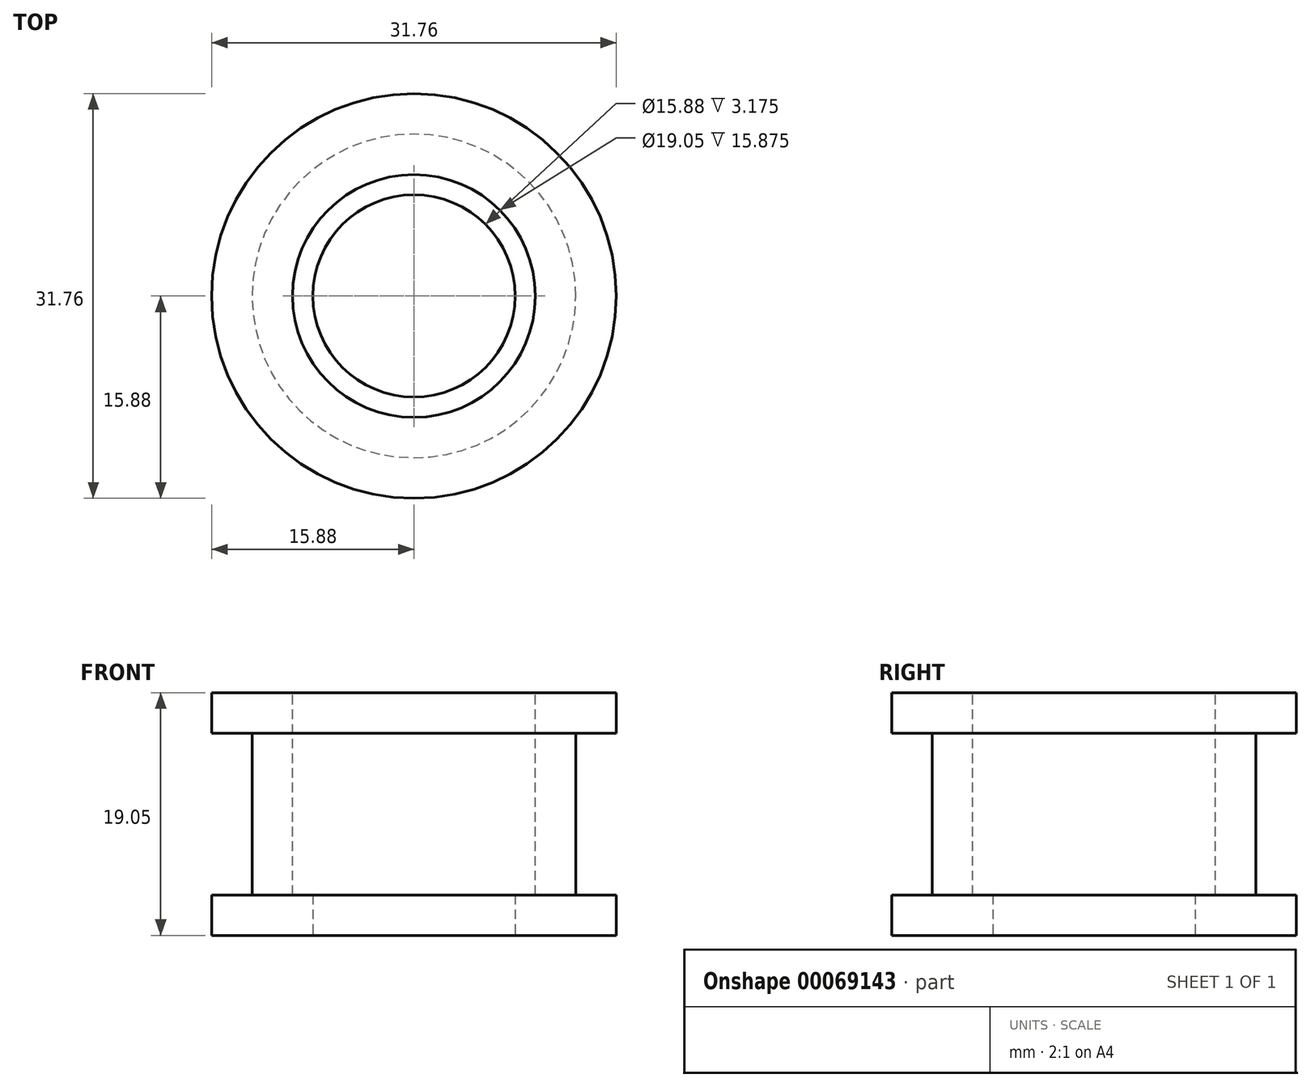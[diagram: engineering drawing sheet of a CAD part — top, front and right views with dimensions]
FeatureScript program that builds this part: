
annotation { "Feature Type Name" : "Feature", "Feature Type Description" : "" }
export const myFeature = defineFeature(function(context is Context, id is Id, definition is map)
    precondition{}
    {
        {
            var Q0;
            Q0=qCreatedBy(makeId("Top.planeOp"),FACE);
            var sketch = newSketch(context, id + "F0", { "sketchPlane" : qUnion([Q0])});
            skCircle(sketch, "E0", {"center": v(0, 0) * mm, "radius": 12.7 * mm});
            skCircle(sketch, "E1", {"center": v(0, 0) * mm, "radius": 7.94 * mm});
            skSolve(sketch);
        }
        {
            var Q0;
            Q0=makeQuery(id+"F0.imprint","IMPRINT",FACE,{"disambiguationData":[TD([[makeQuery(id+"F0.imprint","IMPRINT",EDGE,{"derivedFrom":sQuery(id+"F0.wireOp",EDGE,"E0")}),1.0]])]});
            extrude(context, id + "F1", {"entities" : qUnion([Q0]), "depth" : 19.05 * mm, "offsetDistance" : 25.4 * mm});
        }
        {
            var Q0;
            Q0=makeQuery(id+"F1.opExtrude","CAP_FACE",FACE,{"disambiguationData":[OSD([sQuery(id+"F0.wireOp",EDGE,"E0"),sQuery(id+"F0.wireOp",EDGE,"E1")])],"isStart":false});
            var sketch = newSketch(context, id + "F2", { "sketchPlane" : qUnion([Q0])});
            skCircle(sketch, "E2", {"center": v(0, 0) * mm, "radius": 9.53 * mm});
            skSolve(sketch);
        }
        {
            var Q0;
            Q0=makeQuery(id+"F2.imprint","IMPRINT",FACE,{"disambiguationData":[TD([[makeQuery(id+"F2.imprint","IMPRINT",EDGE,{"derivedFrom":sQuery(id+"F2.wireOp",EDGE,"E2")}),1.0]])]});
            extrude(context, id + "F3", {"entities" : qUnion([Q0]), "operationType" : NewBodyOperationType.REMOVE, "oppositeDirection" : true, "depth" : 15.88 * mm, "offsetDistance" : 25.4 * mm});
        }
        {
            var Q0;
            Q0=makeQuery(id+"F3.boolean.opBoolean","COPY",FACE,{"derivedFrom":makeQuery(id+"F3.opExtrude","CAP_FACE",FACE,{"disambiguationData":[OSD([sQuery(id+"F0.wireOp",EDGE,"E1"),sQuery(id+"F2.wireOp",EDGE,"E2")])],"isStart":false})});
            var sketch = newSketch(context, id + "F4", { "sketchPlane" : qUnion([Q0])});
            skCircle(sketch, "E3", {"center": v(0, 0) * mm, "radius": 15.88 * mm});
            skCircle(sketch, "E4", {"center": v(0, 0) * mm, "radius": 12.7 * mm});
            skSolve(sketch);
        }
        {
            var Q0;
            Q0=makeQuery(id+"F4.imprint","IMPRINT",FACE,{"disambiguationData":[TD([[makeQuery(id+"F4.imprint","IMPRINT",EDGE,{"derivedFrom":sQuery(id+"F4.wireOp",EDGE,"E3")}),1.0]])]});
            extrude(context, id + "F5", {"entities" : qUnion([Q0]), "operationType" : NewBodyOperationType.ADD, "oppositeDirection" : true, "depth" : 3.17 * mm, "offsetDistance" : 25.4 * mm});
        }
        {
            var Q0;
            Q0=makeQuery(id+"F1.opExtrude","CAP_FACE",FACE,{"disambiguationData":[OSD([sQuery(id+"F0.wireOp",EDGE,"E0"),sQuery(id+"F0.wireOp",EDGE,"E1")])],"isStart":false});
            var sketch = newSketch(context, id + "F6", { "sketchPlane" : qUnion([Q0])});
            skCircle(sketch, "E5", {"center": v(0, 0) * mm, "radius": 15.88 * mm});
            skCircle(sketch, "E6", {"center": v(0, 0) * mm, "radius": 12.7 * mm});
            skSolve(sketch);
        }
        {
            var Q0;
            Q0=makeQuery(id+"F6.imprint","IMPRINT",FACE,{"disambiguationData":[TD([[makeQuery(id+"F6.imprint","IMPRINT",EDGE,{"derivedFrom":sQuery(id+"F6.wireOp",EDGE,"E5")}),1.0]])]});
            extrude(context, id + "F7", {"entities" : qUnion([Q0]), "operationType" : NewBodyOperationType.ADD, "oppositeDirection" : true, "depth" : 3.17 * mm, "offsetDistance" : 25.4 * mm});
        }
    });
